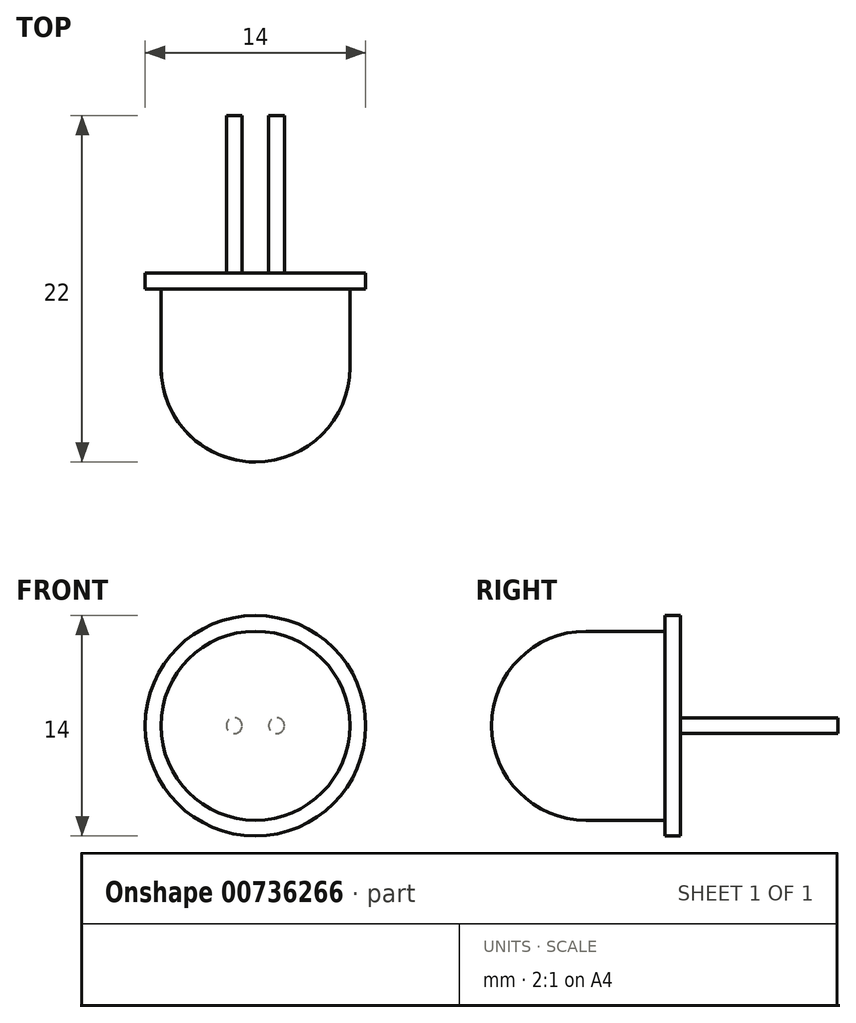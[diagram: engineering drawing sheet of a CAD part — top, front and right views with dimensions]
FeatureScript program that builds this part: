
annotation { "Feature Type Name" : "Feature", "Feature Type Description" : "" }
export const myFeature = defineFeature(function(context is Context, id is Id, definition is map)
    precondition{}
    {
        {
            var Q0;
            Q0=qCreatedBy(makeId("Top.planeOp"),FACE);
            var sketch = newSketch(context, id + "F0", { "sketchPlane" : qUnion([Q0])});
            skLineSegment(sketch, "E0.bottom", {"start": v(0, 0) * mm, "end": v(7, 0) * mm});
            skLineSegment(sketch, "E0.top", {"start": v(0, -1) * mm, "end": v(7, -1) * mm});
            skLineSegment(sketch, "E0.left", {"start": v(0, 0) * mm, "end": v(0, -1) * mm});
            skLineSegment(sketch, "E0.right", {"start": v(7, 0) * mm, "end": v(7, -1) * mm});
            skLineSegment(sketch, "E1.bottom", {"start": v(0, -1) * mm, "end": v(6, -1) * mm});
            skLineSegment(sketch, "E1.top", {"start": v(0, -6) * mm, "end": v(6, -6) * mm});
            skLineSegment(sketch, "E1.left", {"start": v(0, -1) * mm, "end": v(0, -6) * mm});
            skLineSegment(sketch, "E1.right", {"start": v(6, -1) * mm, "end": v(6, -6) * mm});
            skArc(sketch, "E2", {"start": v(6, -6) * mm, "mid": v(4.24, -10.24) * mm, "end": v(0, -12) * mm});
            skLineSegment(sketch, "E3", {"start": v(0, -12) * mm, "end": v(0, -6) * mm});
            skSolve(sketch);
        }
        {
            var Q0;
            Q0=makeQuery(id+"F0.imprint","IMPRINT",FACE,{"disambiguationData":[TD([[makeQuery(id+"F0.imprint","IMPRINT",EDGE,{"derivedFrom":sQuery(id+"F0.wireOp",EDGE,"E0.bottom")}),-1.0]])]});
            var Q1;
            Q1=makeQuery(id+"F0.imprint","IMPRINT",FACE,{"disambiguationData":[TD([[makeQuery(id+"F0.imprint","IMPRINT",EDGE,{"derivedFrom":sQuery(id+"F0.wireOp",EDGE,"E1.top")}),1.0]])]});
            var Q2;
            Q2=makeQuery(id+"F0.imprint","IMPRINT",FACE,{"disambiguationData":[TD([[makeQuery(id+"F0.imprint","IMPRINT",EDGE,{"derivedFrom":sQuery(id+"F0.wireOp",EDGE,"E1.top")}),-1.0]])]});
            var Q3;
            Q3=sQuery(id+"F0.wireOp",EDGE,"E3");
            revolve(context, id + "F1", {"surfaceOperationType" : NewSurfaceOperationType.NEW, "entities" : qUnion([Q0, Q1, Q2]), "axis" : qUnion([Q3]), "revolveType" : RevolveType.FULL});
        }
        {
            var Q0;
            Q0=makeQuery(id+"F1.opRevolve","SWEPT_FACE",FACE,{"disambiguationData":[OSD([sQuery(id+"F0.wireOp",EDGE,"E0.bottom")])]});
            var sketch = newSketch(context, id + "F2", { "sketchPlane" : qUnion([Q0])});
            skLineSegment(sketch, "E4", {"start": v(1.34, 0) * mm, "end": v(-1.34, 0) * mm});
            skPoint(sketch, "E5", {"position": v(0, 0) * mm});
            skCircle(sketch, "E6", {"center": v(-1.34, 0) * mm, "radius": 0.5 * mm});
            skCircle(sketch, "E7", {"center": v(1.34, 0) * mm, "radius": 0.5 * mm});
            skSolve(sketch);
        }
        {
            var Q0;
            Q0 = qSketchRegion(id + "F2", true);
            extrude(context, id + "F3", {"entities" : qUnion([Q0]), "depth" : 10 * mm, "offsetDistance" : 25 * mm});
        }
    });
